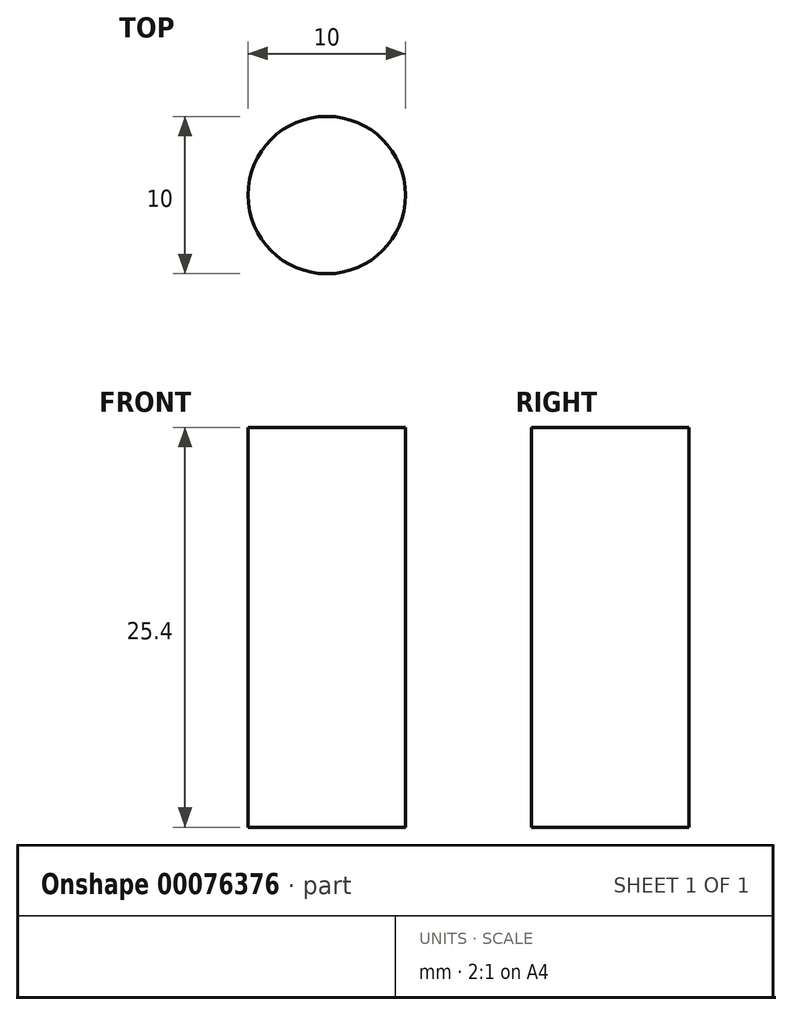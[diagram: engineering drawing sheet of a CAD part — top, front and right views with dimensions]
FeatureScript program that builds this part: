
annotation { "Feature Type Name" : "Feature", "Feature Type Description" : "" }
export const myFeature = defineFeature(function(context is Context, id is Id, definition is map)
    precondition{}
    {
        {
            var Q0;
            Q0=qCreatedBy(makeId("Top.planeOp"),FACE);
            var sketch = newSketch(context, id + "F0", { "sketchPlane" : qUnion([Q0])});
            skCircle(sketch, "E0", {"center": v(0, 0) * mm, "radius": 5 * mm});
            skSolve(sketch);
        }
        {
            var Q0;
            Q0=makeQuery(id+"F0.imprint","IMPRINT",FACE,{"disambiguationData":[TD([[makeQuery(id+"F0.imprint","IMPRINT",EDGE,{"derivedFrom":sQuery(id+"F0.wireOp",EDGE,"E0")}),1.0]])]});
            extrude(context, id + "F1", {"entities" : qUnion([Q0]), "depth" : 25.4 * mm});
        }
    });
